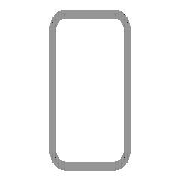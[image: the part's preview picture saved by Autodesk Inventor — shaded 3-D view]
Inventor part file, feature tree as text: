
AUTODESK INVENTOR PART (.ipt)
format: ipt  version: 2025 (Build 290162010, 162A)  size: 133,120 bytes
history: native  units: mm (DEFAULTED — no unit token found)
features: other x4, sketch x1, plane x1
ambient origin geometry x8: Origin, YZ Plane, XZ Plane, XY Plane, X Axis, Y Axis, Z Axis, Center Point
bodies: Solid1 (feature_tree), Body (feature_tree)
feature tree (6):
  parser-record x1  (decoder bookkeeping rows leaked as tree rows — omitted from the tree; the rows remain in map.json)
  other  "Driven Length"
  other  "Start Plane"
  other  "End Plane"
  sketch  "Sketch3"  dims[d3=710.0mm d4=0.0mm d7=6.0mm d9=40.0mm d11=80.0mm d12=3.0mm d13=80.0mm d14=790.0mm d15=20.0mm d16=40.0mm d17=90.0deg d18=710.0mm]
  plane  "Work Plane3"
